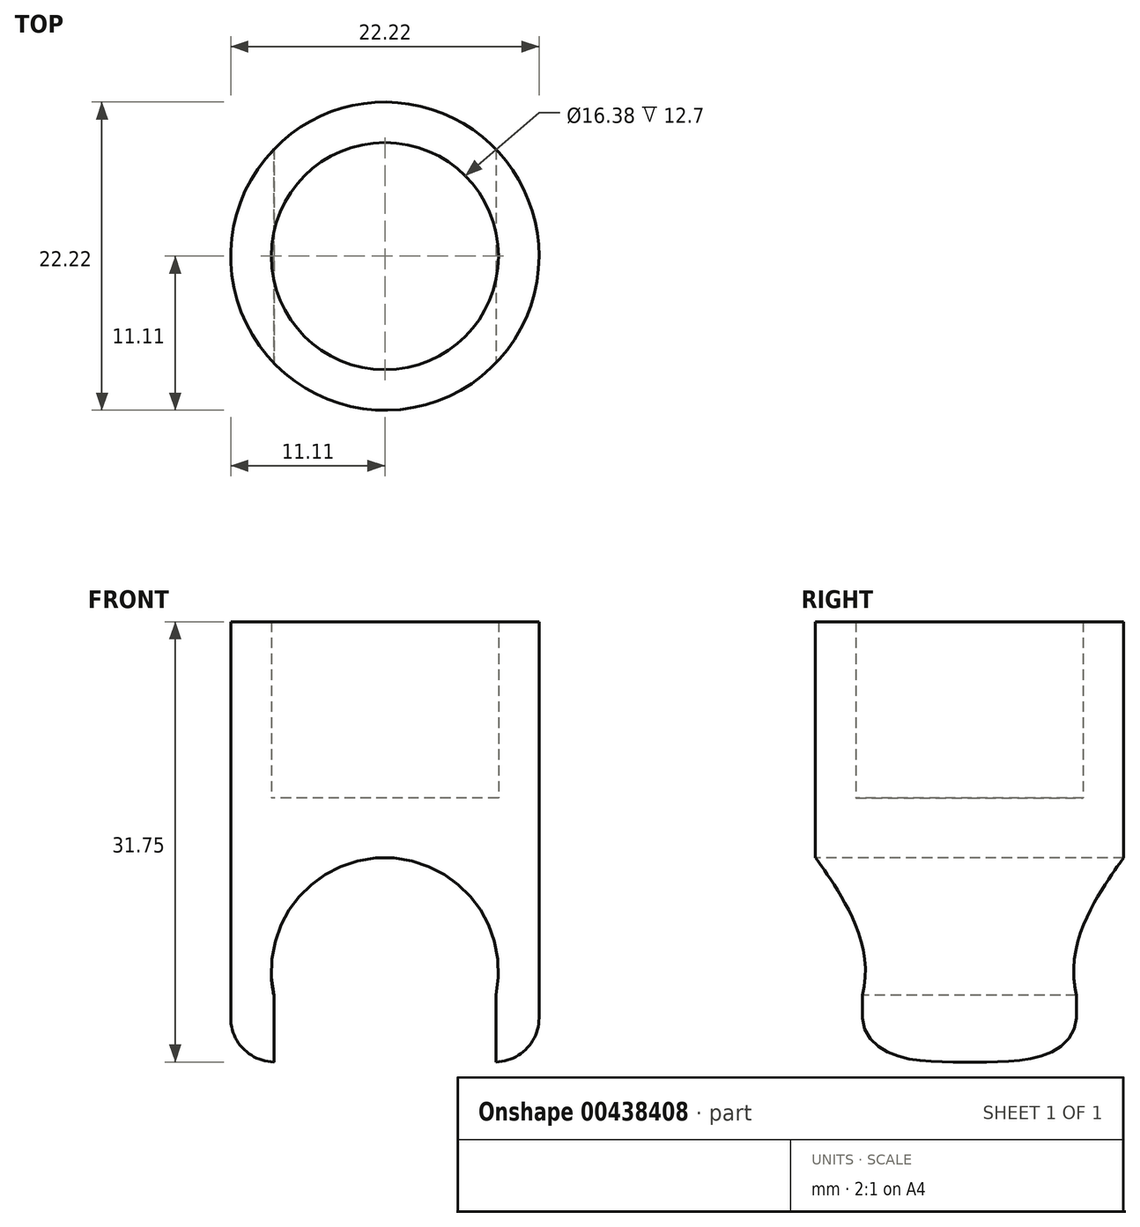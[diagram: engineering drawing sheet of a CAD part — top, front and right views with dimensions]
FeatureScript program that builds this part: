
annotation { "Feature Type Name" : "Feature", "Feature Type Description" : "" }
export const myFeature = defineFeature(function(context is Context, id is Id, definition is map)
    precondition{}
    {
        {
            var Q0;
            Q0=qCreatedBy(makeId("Top.planeOp"),FACE);
            var sketch = newSketch(context, id + "F0", { "sketchPlane" : qUnion([Q0])});
            skCircle(sketch, "E0", {"center": v(0, 0) * mm, "radius": 8.2 * mm});
            skCircle(sketch, "E1", {"center": v(0, 0) * mm, "radius": 11.11 * mm});
            skSolve(sketch);
        }
        {
            var Q0;
            Q0=makeQuery(id+"F0.imprint","IMPRINT",FACE,{"disambiguationData":[TD([[makeQuery(id+"F0.imprint","IMPRINT",EDGE,{"derivedFrom":sQuery(id+"F0.wireOp",EDGE,"E0")}),-1.0]])]});
            extrude(context, id + "F1", {"entities" : qUnion([Q0]), "depth" : 12.7 * mm});
        }
        {
            var Q0;
            Q0=qCreatedBy(makeId("Top.planeOp"),FACE);
            var sketch = newSketch(context, id + "F2", { "sketchPlane" : qUnion([Q0])});
            skCircle(sketch, "E2", {"center": v(0, 0) * mm, "radius": 11.11 * mm});
            skSolve(sketch);
        }
        {
            var Q0;
            Q0=makeQuery(id+"F2.imprint","IMPRINT",FACE,{"disambiguationData":[TD([[makeQuery(id+"F2.imprint","IMPRINT",EDGE,{"derivedFrom":sQuery(id+"F2.wireOp",EDGE,"E2")}),1.0]])]});
            extrude(context, id + "F3", {"entities" : qUnion([Q0]), "operationType" : NewBodyOperationType.ADD, "oppositeDirection" : true, "depth" : 19.05 * mm});
        }
        {
            var Q0;
            Q0=qCreatedBy(makeId("Front.planeOp"),FACE);
            var sketch = newSketch(context, id + "F4", { "sketchPlane" : qUnion([Q0])});
            skArc(sketch, "E3", {"start": v(8, -14.25) * mm, "mid": v(0, -4.31) * mm, "end": v(-8, -14.25) * mm});
            skLineSegment(sketch, "E4", {"start": v(0, 0) * mm, "end": v(0, -18.84) * mm});
            skLineSegment(sketch, "E5", {"start": v(-8, -20.98) * mm, "end": v(8, -20.98) * mm});
            skLineSegment(sketch, "E6.trimOffspring", {"start": v(-8, -14.25) * mm, "end": v(-8, -20.98) * mm});
            skPoint(sketch, "E7.0.start.orphan", {"position": v(-8, 0) * mm});
            skLineSegment(sketch, "E8.trimOffspring", {"start": v(8, -14.25) * mm, "end": v(8, -20.98) * mm});
            skPoint(sketch, "E9.MirrorCS.start.orphan", {"position": v(8, 0) * mm});
            skSolve(sketch);
        }
        {
            var Q0;
            Q0 = qSketchRegion(id + "F4", true);
            extrude(context, id + "F5", {"entities" : qUnion([Q0]), "operationType" : NewBodyOperationType.REMOVE, "endBound" : BoundingType.SYMMETRIC, "oppositeDirection" : true, "depth" : 38.1 * mm});
        }
        {
            var Q0;
            {var subQ0=sQuery(id+"F2.wireOp",EDGE,"E2");Q0=makeQuery(id+"F5.boolean.opBoolean","SPLIT",EDGE,{"disambiguationData":[TD([makeQuery(id+"F5.opExtrude","SWEPT_FACE",FACE,{"disambiguationData":[OSD([sQuery(id+"F4.wireOp",EDGE,"E6.trimOffspring")])]})])],"derivedFrom":makeQuery(id+"F3.opExtrude","CAP_EDGE",EDGE,{"disambiguationData":[OSD([subQ0])],"isStart":false})});}
            var Q1;
            {var subQ0=sQuery(id+"F2.wireOp",EDGE,"E2");Q1=makeQuery(id+"F5.boolean.opBoolean","SPLIT",EDGE,{"disambiguationData":[TD([makeQuery(id+"F5.opExtrude","SWEPT_FACE",FACE,{"disambiguationData":[OSD([sQuery(id+"F4.wireOp",EDGE,"E8.trimOffspring")])]})])],"derivedFrom":makeQuery(id+"F3.opExtrude","CAP_EDGE",EDGE,{"disambiguationData":[OSD([subQ0])],"isStart":false})});}
            fillet(context, id + "F6", {"entities" : qUnion([Q0, Q1]), "radius" : 3.17 * mm, "allowEdgeOverflow" : false});
        }
    });
